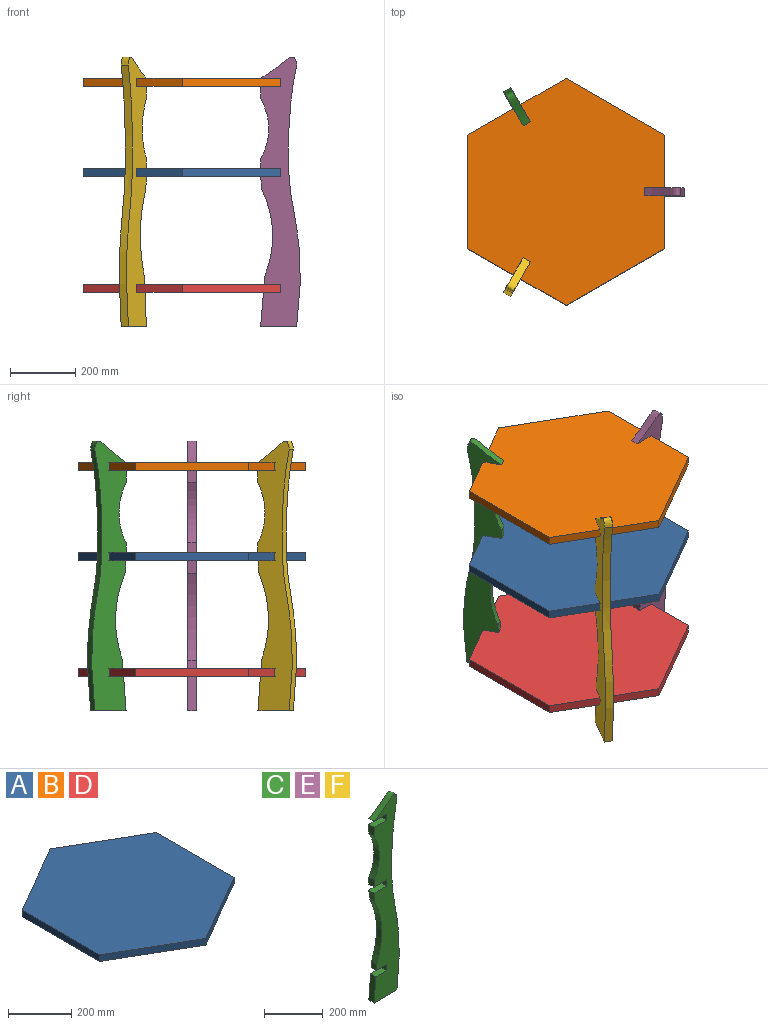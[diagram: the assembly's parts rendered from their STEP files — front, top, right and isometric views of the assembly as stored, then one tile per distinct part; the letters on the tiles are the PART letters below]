
ASSEMBLY  parts=6 mates=6
PART A: 8 faces, bbox 600x692.8x25.4 mm
  f0: plane 300x173.21mm, normal (0.5,0.87,0), area 8798.8mm2, adj f1,f5,f6,f7
  f1: plane 300x173.21mm, normal (-0.5,0.87,0), area 8798.8mm2, adj f0,f2,f6,f7
  f2: plane 346.41x25.4mm, normal (-1,0,0), area 8798.8mm2, adj f1,f3,f6,f7
  f3: plane 300x173.21mm, normal (-0.5,-0.87,0), area 8798.8mm2, adj f2,f4,f6,f7
  f4: plane 300x173.21mm, normal (0.5,-0.87,0), area 8798.8mm2, adj f3,f5,f6,f7
  f5: plane 346.41x25.4mm, normal (1,0,0), area 8798.8mm2, adj f0,f4,f6,f7
  f6: plane 692.82x600mm, normal (0,0,1), area 311769.1mm2, adj f0,f1,f2,f3,f4,f5
  f7: plane 692.82x600mm, normal (0,0,-1), area 311769.1mm2, adj f0,f1,f2,f3,f4,f5
PART B: same geometry as A
PART C: 21 faces, bbox 140.5x25.4x836.6 mm
  f0: plane 36.51x25.4mm, normal (-1,0,0), area 927.4mm2, adj f4,f5,f12,f18
  f1: plane 29.17x25.4mm, normal (-1,0,0), area 740.8mm2, adj f4,f5,f13,f18
  f2: plane 38.96x25.4mm, normal (-1,0,-0.1), area 994.1mm2, adj f4,f5,f15,f17
  f3: plane 25.4x24.58mm, normal (-1,0,0.08), area 626.3mm2, adj f4,f5,f16,f17
  f4: plane 836.59x140.55mm, normal (0,-1,0), area 65500.3mm2, adj f0,f1,f2,f3,f6,f7,f8,f9
  f5: plane 836.59x140.55mm, normal (0,1,0), area 65500.3mm2, adj f0,f1,f2,f3,f6,f7,f8,f9
  f6: plane 25.4x25.4mm, normal (-1,0,0), area 645.2mm2, adj f4,f5,f7,f16
  f7: plane 51.57x25.4mm, normal (0,0,1), area 1309.8mm2, adj f4,f5,f6,f8
  f8: plane 105.43x25.4mm, normal (-1,0,0.08), area 2686.5mm2, adj f4,f5,f7,f9
  f9: plane 110x25.4mm, normal (0,0,-1), area 2794mm2, adj f4,f5,f8,f19
  f10: plane 60x25.4mm, normal (0,0,-1), area 1524mm2, adj f4,f5,f11,f20
  f11: plane 25.4x25.4mm, normal (-1,0,0), area 645.2mm2, adj f4,f5,f10,f12
  f12: plane 60x25.4mm, normal (0,0,1), area 1524mm2, adj f0,f4,f5,f11
  f13: plane 60x25.4mm, normal (0,0,-1), area 1524mm2, adj f1,f4,f5,f14
  f14: plane 25.4x25.4mm, normal (-1,0,0), area 645.2mm2, adj f4,f5,f13,f15
  f15: plane 60x25.4mm, normal (0,0,1), area 1524mm2, adj f2,f4,f5,f14
  f16: plane 49.53x25.4mm, normal (0,0,-1), area 1258.1mm2, adj f3,f4,f5,f6
  f17: extruded ~264.83x33.21mm, area 6935.2mm2, adj f2,f3,f4,f5
  f18: extruded ~184.32x25.4mm, area 4900mm2, adj f0,f1,f4,f5
  f19: extruded ~800x37.19mm, area 20440mm2, adj f4,f5,f9,f20
  f20: extruded ~110x64.53mm, area 3742.6mm2, adj f4,f5,f10,f19
PART D: same geometry as A
PART E: same geometry as C
PART F: same geometry as C
PLACE A t=(-532.6,71.82,-71.85)mm
PLACE B t=(-532.6,71.82,203.55)mm
PLACE C rot(axis=(0,0,1),120deg) t=(-620.49,198.66,78.91)mm
PLACE D t=(-532.6,71.82,-425.62)mm
PLACE E t=(-378.81,84.52,78.91)mm fixed
PLACE F rot(axis=(0,0,-1),120deg) t=(-598.5,-67.71,78.91)mm
MATE planar E.f10 <-> B.f6  axis (0,0,-1) through (-262.6,71.82,228.95)mm
MATE planar A.f5 <-> E.f14  axis (1,0,0) through (-232.6,71.82,-59.15)mm
MATE planar C.f11 <-> B.f1  axis (0.5,-0.87,0) through (-682.6,331.63,216.25)mm
MATE planar E.f11 <-> B.f5  axis (-1,0,0) through (-232.6,71.82,216.25)mm
MATE planar E.f6 <-> D.f5  axis (-1,0,0) through (-232.6,71.82,-412.92)mm
MATE planar F.f11 <-> B.f3  axis (0.5,0.87,0) through (-682.6,-187.98,216.25)mm
